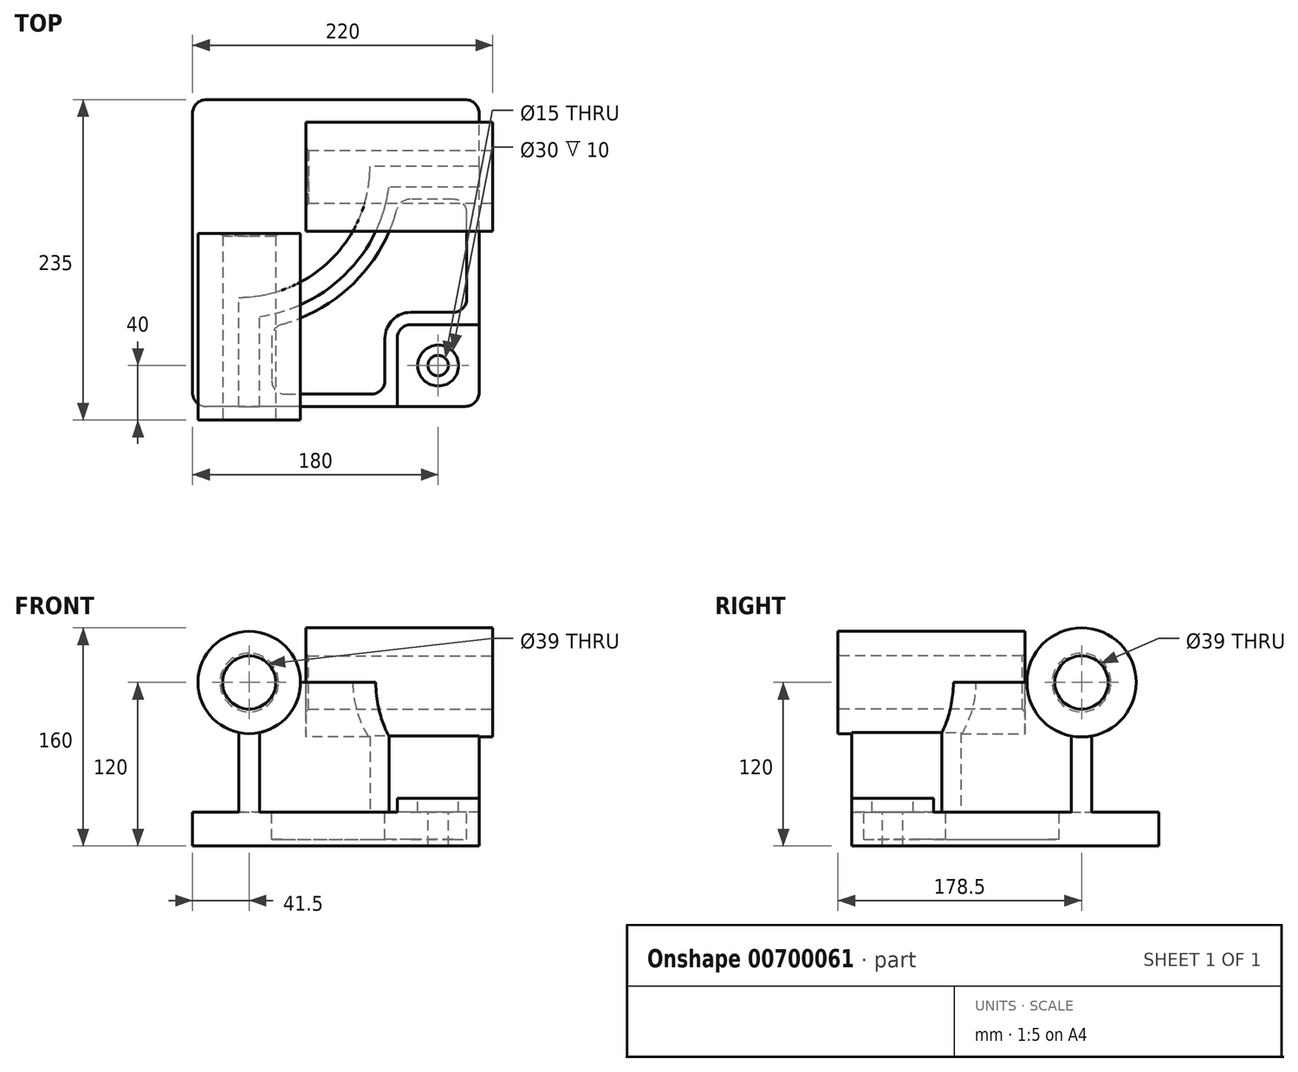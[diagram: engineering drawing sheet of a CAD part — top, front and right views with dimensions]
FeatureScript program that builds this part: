
annotation { "Feature Type Name" : "Feature", "Feature Type Description" : "" }
export const myFeature = defineFeature(function(context is Context, id is Id, definition is map)
    precondition{}
    {
        {
            var Q0;
            Q0=qCreatedBy(makeId("Top.planeOp"),FACE);
            var sketch = newSketch(context, id + "F0", { "sketchPlane" : qUnion([Q0])});
            skLineSegment(sketch, "E0.bottom", {"start": v(105, -112.5) * mm, "end": v(-105, -112.5) * mm});
            skLineSegment(sketch, "E0.top", {"start": v(105, 112.5) * mm, "end": v(-105, 112.5) * mm});
            skLineSegment(sketch, "E0.left", {"start": v(105, -112.5) * mm, "end": v(105, 112.5) * mm});
            skLineSegment(sketch, "E0.right", {"start": v(-105, -112.5) * mm, "end": v(-105, 112.5) * mm});
            skPoint(sketch, "E0.middle", {"position": v(0, 0) * mm});
            skSolve(sketch);
        }
        {
            var Q0;
            Q0=makeQuery(id+"F0.imprint","IMPRINT",FACE,{"disambiguationData":[TD([[makeQuery(id+"F0.imprint","IMPRINT",EDGE,{"derivedFrom":sQuery(id+"F0.wireOp",EDGE,"E0.bottom")}),-1.0]])]});
            extrude(context, id + "F1", {"entities" : qUnion([Q0]), "depth" : 25 * mm, "offsetDistance" : 25 * mm});
        }
        {
            var Q0;
            Q0=makeQuery(id+"F1.opExtrude","CAP_FACE",FACE,{"disambiguationData":[OSD([sQuery(id+"F0.wireOp",EDGE,"E0.bottom"),sQuery(id+"F0.wireOp",EDGE,"E0.top"),sQuery(id+"F0.wireOp",EDGE,"E0.left"),sQuery(id+"F0.wireOp",EDGE,"E0.right")])],"isStart":false});
            var sketch = newSketch(context, id + "F2", { "sketchPlane" : qUnion([Q0])});
            skLineSegment(sketch, "E1", {"start": v(-71, -112.5) * mm, "end": v(-71, -32.5) * mm});
            skLineSegment(sketch, "E2", {"start": v(105, 63.5) * mm, "end": v(25, 63.5) * mm});
            skArc(sketch, "E3", {"start": v(-71, -32.5) * mm, "mid": v(-3.12, -4.38) * mm, "end": v(25, 63.5) * mm});
            skLineSegment(sketch, "E4", {"start": v(-71, 63.5) * mm, "end": v(25, 63.5) * mm, "construction": true});
            skLineSegment(sketch, "E5", {"start": v(-71, 63.5) * mm, "end": v(-71, -32.5) * mm, "construction": true});
            skLineSegment(sketch, "E6.0", {"start": v(-56, -112.5) * mm, "end": v(-56, -46.48) * mm});
            skArc(sketch, "E6.1", {"start": v(-56, -46.48) * mm, "mid": v(7.49, -14.99) * mm, "end": v(38.98, 48.5) * mm});
            skLineSegment(sketch, "E6.2", {"start": v(105, 48.5) * mm, "end": v(38.98, 48.5) * mm});
            skLineSegment(sketch, "E7.0", {"start": v(105, -112.5) * mm, "end": v(105, 112.5) * mm});
            skLineSegment(sketch, "E8.0", {"start": v(105, -112.5) * mm, "end": v(-105, -112.5) * mm});
            skSolve(sketch);
        }
        {
            var Q0;
            {var subQ2=sQuery(id+"F2.wireOp",EDGE,"E1");Q0=makeQuery(id+"F2.imprint","IMPRINT",FACE,{"disambiguationData":[TD([[makeQuery(id+"F2.imprint","IMPRINT",EDGE,{"derivedFrom":subQ2}),-1.0]])]});}
            extrude(context, id + "F3", {"entities" : qUnion([Q0]), "operationType" : NewBodyOperationType.ADD, "depth" : 95 * mm, "offsetDistance" : 25 * mm});
        }
        {
            var Q0;
            Q0=makeQuery(id+"F3.boolean.opBoolean","MERGE",FACE,{"derivedFrom":[makeQuery(id+"F1.opExtrude","SWEPT_FACE",FACE,{"disambiguationData":[OSD([sQuery(id+"F0.wireOp",EDGE,"E0.bottom")])]}),makeQuery(id+"F3.opExtrude","SWEPT_FACE",FACE,{"disambiguationData":[OSD([sQuery(id+"F2.wireOp",EDGE,"E8.0")])]})]});
            var sketch = newSketch(context, id + "F4", { "sketchPlane" : qUnion([Q0])});
            skCircle(sketch, "E9", {"center": v(-63.5, 120) * mm, "radius": 37.5 * mm});
            skSolve(sketch);
        }
        {
            var Q0;
            Q0 = qSketchRegion(id + "F4", true);
            extrude(context, id + "F5", {"entities" : qUnion([Q0]), "operationType" : NewBodyOperationType.ADD, "depth" : 10 * mm, "offsetDistance" : 25 * mm, "hasSecondDirection" : true, "secondDirectionOppositeDirection" : true, "secondDirectionDepth" : (137 - 10) * mm});
        }
        {
            var Q0;
            Q0=makeQuery(id+"F3.boolean.opBoolean","MERGE",FACE,{"derivedFrom":[makeQuery(id+"F1.opExtrude","SWEPT_FACE",FACE,{"disambiguationData":[OSD([sQuery(id+"F0.wireOp",EDGE,"E0.left")])]}),makeQuery(id+"F3.opExtrude","SWEPT_FACE",FACE,{"disambiguationData":[OSD([sQuery(id+"F2.wireOp",EDGE,"E7.0")])]})]});
            var sketch = newSketch(context, id + "F6", { "sketchPlane" : qUnion([Q0])});
            skCircle(sketch, "E10", {"center": v(56, 120) * mm, "radius": 40 * mm});
            skSolve(sketch);
        }
        {
            var Q0;
            Q0 = qSketchRegion(id + "F6", true);
            extrude(context, id + "F7", {"entities" : qUnion([Q0]), "operationType" : NewBodyOperationType.ADD, "depth" : 10 * mm, "offsetDistance" : 25 * mm, "hasSecondDirection" : true, "secondDirectionOppositeDirection" : true, "secondDirectionDepth" : (137 - 10) * mm});
        }
        {
            var Q0;
            {var subQ0=sQuery(id+"F0.wireOp",EDGE,"E0.left");var subQ1=sQuery(id+"F0.wireOp",EDGE,"E0.bottom");Q0=makeQuery(id+"F3.boolean.opBoolean","SPLIT",FACE,{"disambiguationData":[TD([makeQuery(id+"F3.opExtrude","SWEPT_FACE",FACE,{"disambiguationData":[OSD([sQuery(id+"F2.wireOp",EDGE,"E6.0")])]})])],"derivedFrom":makeQuery(id+"F1.opExtrude","CAP_FACE",FACE,{"disambiguationData":[OSD([subQ1,sQuery(id+"F0.wireOp",EDGE,"E0.top"),subQ0,sQuery(id+"F0.wireOp",EDGE,"E0.right")])],"isStart":false})});}
            var sketch = newSketch(context, id + "F8", { "sketchPlane" : qUnion([Q0])});
            skLineSegment(sketch, "E11.bottom", {"start": v(105, -112.5) * mm, "end": v(45, -112.5) * mm});
            skLineSegment(sketch, "E11.top", {"start": v(105, -52.5) * mm, "end": v(45, -52.5) * mm});
            skLineSegment(sketch, "E11.left", {"start": v(105, -112.5) * mm, "end": v(105, -52.5) * mm});
            skLineSegment(sketch, "E11.right", {"start": v(45, -112.5) * mm, "end": v(45, -52.5) * mm});
            skSolve(sketch);
        }
        {
            var Q0;
            Q0 = qSketchRegion(id + "F8", true);
            extrude(context, id + "F9", {"entities" : qUnion([Q0]), "operationType" : NewBodyOperationType.ADD, "depth" : 10 * mm, "offsetDistance" : 25 * mm});
        }
        {
            var Q0;
            Q0=makeQuery(id+"F9.opExtrude","SWEPT_EDGE",EDGE,{"disambiguationData":[OSD([sQuery(id+"F8.wireOp",EDGE,"E11.top"),sQuery(id+"F8.wireOp",EDGE,"E11.right")])]});
            fillet(context, id + "F10", {"entities" : qUnion([Q0]), "radius" : 10 * mm, "tangentPropagation" : true, "allowEdgeOverflow" : false});
        }
        {
            var Q0;
            {var subQ0=sQuery(id+"F0.wireOp",EDGE,"E0.left");var subQ1=sQuery(id+"F0.wireOp",EDGE,"E0.bottom");Q0=makeQuery(id+"F3.boolean.opBoolean","SPLIT",FACE,{"disambiguationData":[TD([makeQuery(id+"F3.opExtrude","SWEPT_FACE",FACE,{"disambiguationData":[OSD([sQuery(id+"F2.wireOp",EDGE,"E6.0")])]})])],"derivedFrom":makeQuery(id+"F1.opExtrude","CAP_FACE",FACE,{"disambiguationData":[OSD([subQ1,sQuery(id+"F0.wireOp",EDGE,"E0.top"),subQ0,sQuery(id+"F0.wireOp",EDGE,"E0.right")])],"isStart":false})});}
            var sketch = newSketch(context, id + "F11", { "sketchPlane" : qUnion([Q0])});
            skLineSegment(sketch, "E12.0", {"start": v(-47, -54.08) * mm, "end": v(-47, -103.5) * mm});
            skArc(sketch, "E12.1", {"start": v(46.58, 39.5) * mm, "mid": v(13.85, -21.35) * mm, "end": v(-47, -54.08) * mm});
            skLineSegment(sketch, "E12.2", {"start": v(-47, -103.5) * mm, "end": v(36, -103.5) * mm});
            skLineSegment(sketch, "E12.3", {"start": v(96, 39.5) * mm, "end": v(46.58, 39.5) * mm});
            skLineSegment(sketch, "E12.4", {"start": v(36, -103.5) * mm, "end": v(36, -62.5) * mm});
            skArc(sketch, "E12.5", {"start": v(36, -62.5) * mm, "mid": v(41.56, -49.06) * mm, "end": v(55, -43.5) * mm});
            skLineSegment(sketch, "E12.6", {"start": v(55, -43.5) * mm, "end": v(96, -43.5) * mm});
            skLineSegment(sketch, "E12.7", {"start": v(96, -43.5) * mm, "end": v(96, 39.5) * mm});
            skSolve(sketch);
        }
        {
            var Q0;
            Q0=makeQuery(id+"F11.imprint","IMPRINT",FACE,{"disambiguationData":[TD([[makeQuery(id+"F11.imprint","IMPRINT",EDGE,{"derivedFrom":sQuery(id+"F11.wireOp",EDGE,"E12.0")}),1.0]])]});
            extrude(context, id + "F12", {"entities" : qUnion([Q0]), "operationType" : NewBodyOperationType.REMOVE, "oppositeDirection" : true, "depth" : (25 - 5) * mm, "offsetDistance" : 25 * mm});
        }
        {
            var Q0;
            Q0=makeQuery(id+"F9.opExtrude","CAP_FACE",FACE,{"disambiguationData":[OSD([sQuery(id+"F8.wireOp",EDGE,"E11.bottom"),sQuery(id+"F8.wireOp",EDGE,"E11.top"),sQuery(id+"F8.wireOp",EDGE,"E11.left"),sQuery(id+"F8.wireOp",EDGE,"E11.right")])],"isStart":false});
            var sketch = newSketch(context, id + "F13", { "sketchPlane" : qUnion([Q0])});
            skCircle(sketch, "E13", {"center": v(75, -82.5) * mm, "radius": 15 * mm});
            skSolve(sketch);
        }
        {
            var Q0;
            Q0=sQuery(id+"F13.wireOp",VERTEX,"E13.center");
            var Q1;
            Q1=makeQuery(id+"F1.opExtrude","SWEPT_BODY",BODY,{"disambiguationData":[OSD([sQuery(id+"F0.wireOp",EDGE,"E0.bottom"),sQuery(id+"F0.wireOp",EDGE,"E0.top"),sQuery(id+"F0.wireOp",EDGE,"E0.left"),sQuery(id+"F0.wireOp",EDGE,"E0.right")])]});
            hole(context, id + "F14", {"style" : HoleStyle.C_BORE, "endStyle" : HoleEndStyle.THROUGH, "holeDiameter" : 15 * mm, "cBoreDiameter" : 30 * mm, "cBoreDepth" : 10 * mm, "majorDiameter" : 5 * mm, "isTappedThrough" : true, "tappedDepth" : 12 * mm, "tapClearance" : 3, "locations" : qUnion([Q0]), "scope" : qUnion([Q1])});
        }
        {
            var Q0;
            Q0=makeQuery(id+"F12.boolean.opBoolean","COPY",EDGE,{"derivedFrom":makeQuery(id+"F12.opExtrude","SWEPT_EDGE",EDGE,{"disambiguationData":[OSD([sQuery(id+"F11.wireOp",EDGE,"E12.0"),sQuery(id+"F11.wireOp",EDGE,"E12.1")])]})});
            var Q1;
            Q1=makeQuery(id+"F12.boolean.opBoolean","COPY",EDGE,{"derivedFrom":makeQuery(id+"F12.opExtrude","SWEPT_EDGE",EDGE,{"disambiguationData":[OSD([sQuery(id+"F11.wireOp",EDGE,"E12.1"),sQuery(id+"F11.wireOp",EDGE,"E12.3")])]})});
            var Q2;
            Q2=makeQuery(id+"F12.boolean.opBoolean","COPY",EDGE,{"derivedFrom":makeQuery(id+"F12.opExtrude","SWEPT_EDGE",EDGE,{"disambiguationData":[OSD([sQuery(id+"F11.wireOp",EDGE,"E12.3"),sQuery(id+"F11.wireOp",EDGE,"E12.7")])]})});
            var Q3;
            Q3=makeQuery(id+"F12.boolean.opBoolean","COPY",EDGE,{"derivedFrom":makeQuery(id+"F12.opExtrude","SWEPT_EDGE",EDGE,{"disambiguationData":[OSD([sQuery(id+"F11.wireOp",EDGE,"E12.6"),sQuery(id+"F11.wireOp",EDGE,"E12.7")])]})});
            var Q4;
            Q4=makeQuery(id+"F12.boolean.opBoolean","COPY",EDGE,{"derivedFrom":makeQuery(id+"F12.opExtrude","SWEPT_EDGE",EDGE,{"disambiguationData":[OSD([sQuery(id+"F11.wireOp",EDGE,"E12.0"),sQuery(id+"F11.wireOp",EDGE,"E12.2")])]})});
            var Q5;
            Q5=makeQuery(id+"F12.boolean.opBoolean","COPY",EDGE,{"derivedFrom":makeQuery(id+"F12.opExtrude","SWEPT_EDGE",EDGE,{"disambiguationData":[OSD([sQuery(id+"F11.wireOp",EDGE,"E12.2"),sQuery(id+"F11.wireOp",EDGE,"E12.4")])]})});
            fillet(context, id + "F15", {"entities" : qUnion([Q0, Q1, Q2, Q3, Q4, Q5]), "radius" : 10 * mm, "tangentPropagation" : true, "allowEdgeOverflow" : false});
        }
        {
            var Q0;
            Q0=makeQuery(id+"F5.opExtrude","CAP_FACE",FACE,{"disambiguationData":[OSD([sQuery(id+"F4.wireOp",EDGE,"E9")])],"isStart":false});
            var sketch = newSketch(context, id + "F16", { "sketchPlane" : qUnion([Q0])});
            skCircle(sketch, "E14", {"center": v(-63.5, 120) * mm, "radius": 19.5 * mm});
            skSolve(sketch);
        }
        {
            var Q0;
            Q0 = qSketchRegion(id + "F16", true);
            extrude(context, id + "F17", {"entities" : qUnion([Q0]), "operationType" : NewBodyOperationType.REMOVE, "endBound" : BoundingType.THROUGH_ALL, "oppositeDirection" : true, "depth" : 25 * mm, "offsetDistance" : 25 * mm});
        }
        {
            var Q0;
            Q0=makeQuery(id+"F7.opExtrude","CAP_FACE",FACE,{"disambiguationData":[OSD([sQuery(id+"F6.wireOp",EDGE,"E10")])],"isStart":false});
            var sketch = newSketch(context, id + "F18", { "sketchPlane" : qUnion([Q0])});
            skCircle(sketch, "E15", {"center": v(56, 120) * mm, "radius": 19.5 * mm});
            skSolve(sketch);
        }
        {
            var Q0;
            Q0 = qSketchRegion(id + "F18", true);
            extrude(context, id + "F19", {"entities" : qUnion([Q0]), "operationType" : NewBodyOperationType.REMOVE, "endBound" : BoundingType.THROUGH_ALL, "oppositeDirection" : true, "depth" : 25 * mm, "offsetDistance" : 25 * mm});
        }
        {
            var Q0;
            Q0=makeQuery(id+"F17.boolean.opBoolean","COPY",EDGE,{"derivedFrom":makeQuery(id+"F17.opExtrude","CAP_EDGE",EDGE,{"disambiguationData":[OSD([sQuery(id+"F16.wireOp",EDGE,"E14")])],"isStart":true})});
            var Q1;
            Q1=makeQuery(id+"F19.boolean.opBoolean","COPY",EDGE,{"derivedFrom":makeQuery(id+"F19.opExtrude","CAP_EDGE",EDGE,{"disambiguationData":[OSD([sQuery(id+"F18.wireOp",EDGE,"E15")])],"isStart":true})});
            var Q2;
            Q2=makeQuery(id+"F17.boolean.opBoolean","INTERSECT",EDGE,{"derivedFrom":[makeQuery(id+"F5.opExtrude","CAP_FACE",FACE,{"disambiguationData":[OSD([sQuery(id+"F4.wireOp",EDGE,"E9")])],"isStart":true}),makeQuery(id+"F17.opExtrude","SWEPT_FACE",FACE,{"disambiguationData":[OSD([sQuery(id+"F16.wireOp",EDGE,"E14")])]})]});
            var Q3;
            Q3=makeQuery(id+"F19.boolean.opBoolean","INTERSECT",EDGE,{"derivedFrom":[makeQuery(id+"F7.opExtrude","CAP_FACE",FACE,{"disambiguationData":[OSD([sQuery(id+"F6.wireOp",EDGE,"E10")])],"isStart":true}),makeQuery(id+"F19.opExtrude","SWEPT_FACE",FACE,{"disambiguationData":[OSD([sQuery(id+"F18.wireOp",EDGE,"E15")])]})]});
            chamfer(context, id + "F20", {"entities" : qUnion([Q0, Q1, Q2, Q3]), "width" : 2 * mm, "tangentPropagation" : true});
        }
        {
            var Q0;
            Q0=makeQuery(id+"F9.boolean.opBoolean","MERGE",EDGE,{"derivedFrom":[makeQuery(id+"F1.opExtrude","SWEPT_EDGE",EDGE,{"disambiguationData":[OSD([sQuery(id+"F0.wireOp",EDGE,"E0.bottom"),sQuery(id+"F0.wireOp",EDGE,"E0.left")])]}),makeQuery(id+"F9.opExtrude","SWEPT_EDGE",EDGE,{"disambiguationData":[OSD([sQuery(id+"F8.wireOp",EDGE,"E11.bottom"),sQuery(id+"F8.wireOp",EDGE,"E11.left")])]})]});
            var Q1;
            Q1=makeQuery(id+"F1.opExtrude","SWEPT_EDGE",EDGE,{"disambiguationData":[OSD([sQuery(id+"F0.wireOp",EDGE,"E0.top"),sQuery(id+"F0.wireOp",EDGE,"E0.left")])]});
            var Q2;
            Q2=makeQuery(id+"F1.opExtrude","SWEPT_EDGE",EDGE,{"disambiguationData":[OSD([sQuery(id+"F0.wireOp",EDGE,"E0.bottom"),sQuery(id+"F0.wireOp",EDGE,"E0.right")])]});
            var Q3;
            Q3=makeQuery(id+"F1.opExtrude","SWEPT_EDGE",EDGE,{"disambiguationData":[OSD([sQuery(id+"F0.wireOp",EDGE,"E0.top"),sQuery(id+"F0.wireOp",EDGE,"E0.right")])]});
            fillet(context, id + "F21", {"entities" : qUnion([Q0, Q1, Q2, Q3]), "radius" : 10 * mm, "tangentPropagation" : true, "allowEdgeOverflow" : false});
        }
    });
